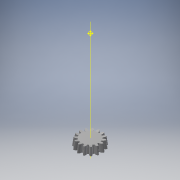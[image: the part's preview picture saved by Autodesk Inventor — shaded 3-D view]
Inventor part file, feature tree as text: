
AUTODESK INVENTOR PART (.ipt)
format: ipt  version: 2017 (Build 210142000, 142)  size: 513,024 bytes
history: native  units: mm
features: other x24, loft x2, pattern_circular x2, sketch x1
ambient origin geometry x6: Origin, XZ Plane, X Axis, Y Axis, Z Axis, Center Point
bodies: Solid1 (feature_tree)
feature tree (29):
  other  "Top Point"
  other  "Mesh Plane2"
  other  "Teeth Body"
  other  "Start Point"
  other  "Tooth Plane"
  other  "Start Sketch"
  other  "End Point"
  other  "3D Sketch Right"
  other  "End Plane Right"
  loft  "Loft Right"
  pattern_circular  "Circular Pattern Right"  [2 undecoded]
  other  "3D Sketch Left"
  other  "End Plane Left"
  loft  "Loft Left"
  pattern_circular  "Circular Pattern Left"  [2 undecoded]
  other  "Fix Body"
  other  "Mesh Plane"
  other  "Top Plane"
  other  "Teeth Body Sketch"
  other  "End Plane"
  other  "End Sketch"
  other  "Helical Curve Left"
  other  "End Sketch Left"
  other  "Body Sketch"
  sketch  "Sketch6"  dims[d0=38.1mm d1=32.044179mm d2=42.954701mm d3=12.7mm d4=164.819921mm d5=90.0deg d7=7.248858mm d8=8.457324mm d9=15.796036mm d11=12.974573mm d12=6.690202mm d15=7.805534mm d16=14.578664mm d17=0.0mm d18=90.0deg d19=0.0mm d20=90.0deg d21=150.0mm d22=360.0deg d26=408.108672mm d27=12.889057mm d28=38.1mm d29=-1.148766mm d30=6.690202mm d31=7.805534mm d32=14.578664mm d35=0.0mm d37=0.0mm d39=0.0mm d40=90.0deg d41=150.0mm d42=360.0deg d46=90.0deg d47=90.0deg d48=0.0mm d49=0.0mm d50=90.0deg d51=2.094395mm d52=0.0mm d53=0.0mm d54=0.0mm d56=19.70544mm d57=23.267285mm d58=15.469418mm d59=21.474118mm d60=14.277218mm d61=21.474118mm d62=14.277218mm d63=90.0deg d64=90.0deg d65=408.108672mm d66=31.5mm d67=38.1mm d68=-1.148766mm d69=12.889057mm d70=7.805534mm d71=14.578664mm d72=6.690202mm d73=14.277218mm d74=21.474118mm d75=0.0mm d76=90.0deg d77=0.0mm d78=90.0deg d79=0.0mm d80=90.0deg d81=150.0mm d82=360.0deg d84=10.0mm d85=20.0mm d86=20.0mm d87=10.0mm d88=0.0mm d89=0.0mm]
  other  "Srf1"
  other  "Helical Curve Right"
  other  "End Sketch Right"
  other  "Pitch Diameter"
note: 4 required parameter values undecoded (feature->parameter linkage not recoverable at this tier; creation-order binding heuristic only, values carry confidence <= 0.55)
